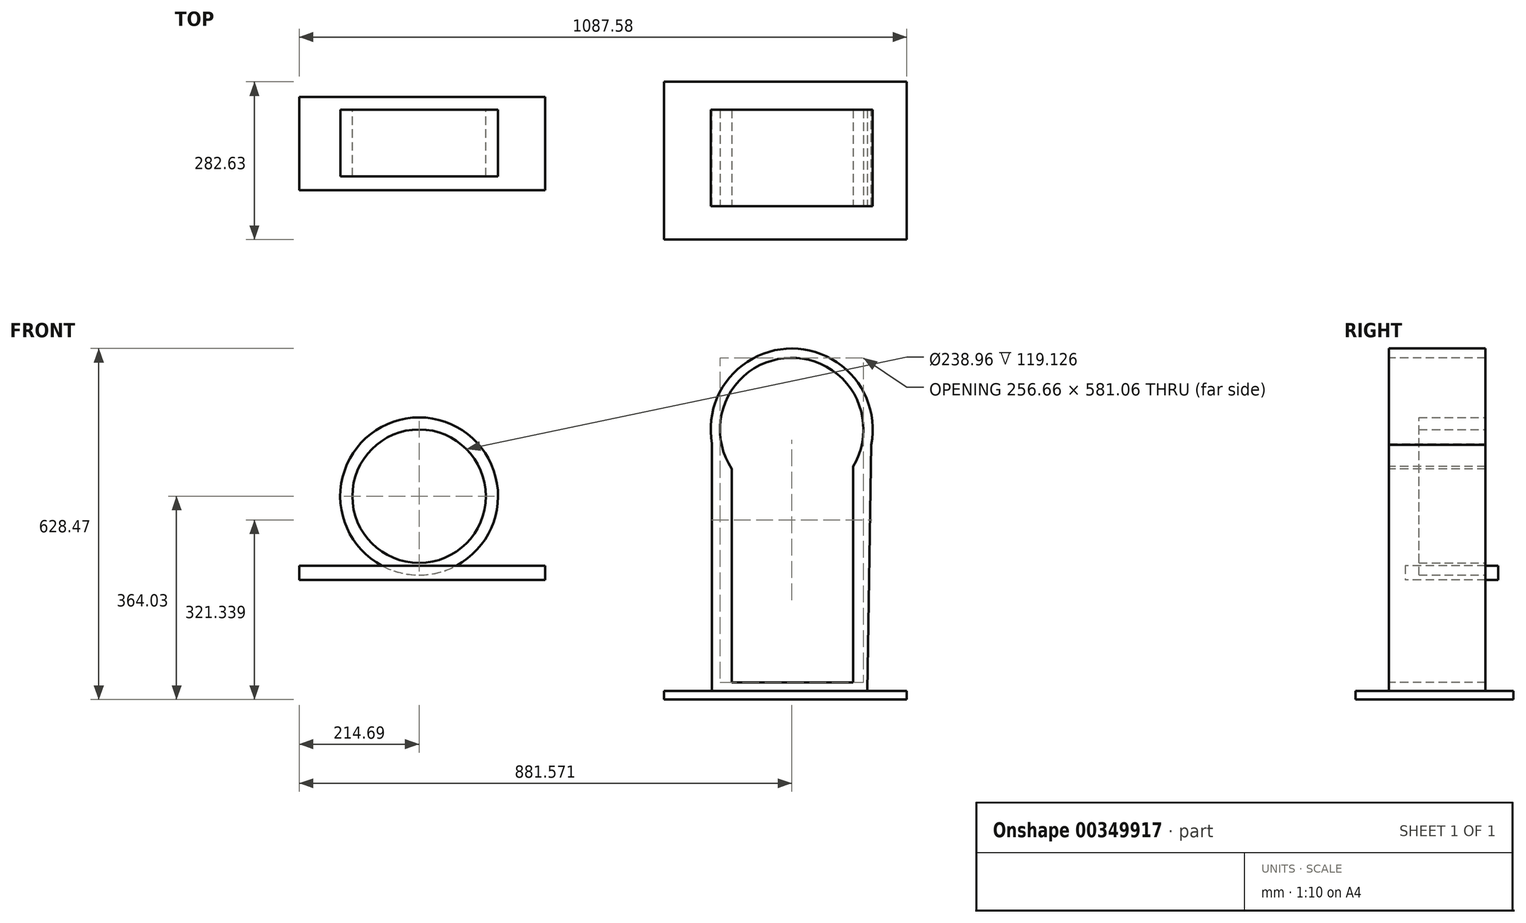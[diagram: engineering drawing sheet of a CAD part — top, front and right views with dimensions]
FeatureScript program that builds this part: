
annotation { "Feature Type Name" : "Feature", "Feature Type Description" : "" }
export const myFeature = defineFeature(function(context is Context, id is Id, definition is map)
    precondition{}
    {
        {
            var Q0;
            Q0=qCreatedBy(makeId("Front.planeOp"),FACE);
            var sketch = newSketch(context, id + "F0", { "sketchPlane" : qUnion([Q0])});
            skCircle(sketch, "E0", {"center": v(0, 0) * mm, "radius": 141.18 * mm});
            skCircle(sketch, "E1", {"center": v(0, 0) * mm, "radius": 119.48 * mm});
            skSolve(sketch);
        }
        {
            var Q0;
            Q0 = qSketchRegion(id + "F0", true);
            extrude(context, id + "F1", {"entities" : qUnion([Q0]), "depth" : 119.13 * mm, "offsetDistance" : 25.4 * mm});
        }
        {
            var Q0;
            Q0=qCreatedBy(makeId("Top.planeOp"),FACE);
            var sketch = newSketch(context, id + "F2", { "sketchPlane" : qUnion([Q0])});
            skLineSegment(sketch, "E2.bottom", {"start": v(247.6, 0) * mm, "end": v(687.7, 0) * mm});
            skLineSegment(sketch, "E2.top", {"start": v(247.6, -166.91) * mm, "end": v(687.7, -166.91) * mm});
            skLineSegment(sketch, "E2.left", {"start": v(247.6, 0) * mm, "end": v(247.6, -166.91) * mm});
            skLineSegment(sketch, "E2.right", {"start": v(687.7, 0) * mm, "end": v(687.7, -166.91) * mm});
            skSolve(sketch);
        }
        {
            var Q0;
            Q0 = qSketchRegion(id + "F2", true);
            extrude(context, id + "F3", {"entities" : qUnion([Q0]), "depth" : 25.4 * mm, "offsetDistance" : 25.4 * mm});
        }
        {
            var Q0;
            Q0=makeQuery(id+"F3.opExtrude","SWEPT_BODY",BODY,{"disambiguationData":[OSD([sQuery(id+"F2.wireOp",EDGE,"E2.bottom"),sQuery(id+"F2.wireOp",EDGE,"E2.top"),sQuery(id+"F2.wireOp",EDGE,"E2.left"),sQuery(id+"F2.wireOp",EDGE,"E2.right")])]});
            transform(context, id + "F4", {"entities" : qUnion([Q0]), "transformType" : TransformType.TRANSLATION_3D, "dx" : -462.28 * mm, "dy" : 22.86 * mm, "dz" : -149.86 * mm, "makeCopy" : false});
        }
        {
            var Q0;
            Q0=qCreatedBy(makeId("Front.planeOp"),FACE);
            var sketch = newSketch(context, id + "F5", { "sketchPlane" : qUnion([Q0])});
            skCircle(sketch, "E3", {"center": v(666.8, 119.45) * mm, "radius": 144.99 * mm});
            skLineSegment(sketch, "E4", {"start": v(524.1, 145.11) * mm, "end": v(524.1, -364.03) * mm});
            skLineSegment(sketch, "E5", {"start": v(524.1, -364.03) * mm, "end": v(801.88, -364.03) * mm});
            skLineSegment(sketch, "E6", {"start": v(801.88, -364.03) * mm, "end": v(810, 142.13) * mm});
            skLineSegment(sketch, "E7", {"start": v(810, 142.13) * mm, "end": v(524.1, 145.11) * mm});
            skSolve(sketch);
        }
        {
            var Q0;
            Q0 = qSketchRegion(id + "F5", true);
            extrude(context, id + "F6", {"entities" : qUnion([Q0]), "depth" : 172.72 * mm, "offsetDistance" : 25.4 * mm});
        }
        {
            var Q0;
            Q0=makeQuery(id+"F6.opExtrude","CAP_FACE",FACE,{"disambiguationData":[OSD([sQuery(id+"F5.wireOp",EDGE,"E3"),sQuery(id+"F5.wireOp",EDGE,"E4"),sQuery(id+"F5.wireOp",EDGE,"E5"),sQuery(id+"F5.wireOp",EDGE,"E6")])],"isStart":false});
            var sketch = newSketch(context, id + "F7", { "sketchPlane" : qUnion([Q0])});
            skCircle(sketch, "E8", {"center": v(666.8, 119.45) * mm, "radius": 128.41 * mm});
            skSolve(sketch);
        }
        {
            var Q0;
            Q0 = qSketchRegion(id + "F7", true);
            extrude(context, id + "F8", {"entities" : qUnion([Q0]), "operationType" : NewBodyOperationType.REMOVE, "oppositeDirection" : true, "depth" : 304.8 * mm, "offsetDistance" : 25.4 * mm});
        }
        {
            var Q0;
            Q0=makeQuery(id+"F6.opExtrude","CAP_FACE",FACE,{"disambiguationData":[OSD([sQuery(id+"F5.wireOp",EDGE,"E3"),sQuery(id+"F5.wireOp",EDGE,"E4"),sQuery(id+"F5.wireOp",EDGE,"E5"),sQuery(id+"F5.wireOp",EDGE,"E6")])],"isStart":false});
            var sketch = newSketch(context, id + "F9", { "sketchPlane" : qUnion([Q0])});
            skLineSegment(sketch, "E9.bottom", {"start": v(559.65, 81.07) * mm, "end": v(776.72, 81.07) * mm});
            skLineSegment(sketch, "E9.top", {"start": v(559.65, -333.22) * mm, "end": v(776.72, -333.22) * mm});
            skLineSegment(sketch, "E9.left", {"start": v(559.65, 81.07) * mm, "end": v(559.65, -333.22) * mm});
            skLineSegment(sketch, "E9.right", {"start": v(776.72, 81.07) * mm, "end": v(776.72, -333.22) * mm});
            skSolve(sketch);
        }
        {
            var Q0;
            Q0 = qSketchRegion(id + "F9", true);
            extrude(context, id + "F10", {"entities" : qUnion([Q0]), "operationType" : NewBodyOperationType.REMOVE, "oppositeDirection" : true, "depth" : 292.1 * mm, "offsetDistance" : 25.4 * mm});
        }
        {
            var Q0;
            Q0=makeQuery(id+"F6.opExtrude","SWEPT_FACE",FACE,{"disambiguationData":[OSD([sQuery(id+"F5.wireOp",EDGE,"E5")])]});
            var sketch = newSketch(context, id + "F11", { "sketchPlane" : qUnion([Q0])});
            skLineSegment(sketch, "E10.bottom", {"start": v(872.89, -50) * mm, "end": v(438.17, -50) * mm});
            skLineSegment(sketch, "E10.top", {"start": v(872.89, 232.63) * mm, "end": v(438.17, 232.63) * mm});
            skLineSegment(sketch, "E10.left", {"start": v(872.89, -50) * mm, "end": v(872.89, 232.63) * mm});
            skLineSegment(sketch, "E10.right", {"start": v(438.17, -50) * mm, "end": v(438.17, 232.63) * mm});
            skPoint(sketch, "E10.middle", {"position": v(655.53, 91.31) * mm});
            skSolve(sketch);
        }
        {
            var Q0;
            Q0 = qSketchRegion(id + "F11", true);
            extrude(context, id + "F12", {"entities" : qUnion([Q0]), "operationType" : NewBodyOperationType.ADD, "oppositeDirection" : true, "depth" : 15.24 * mm, "offsetDistance" : 25.4 * mm});
        }
    });
